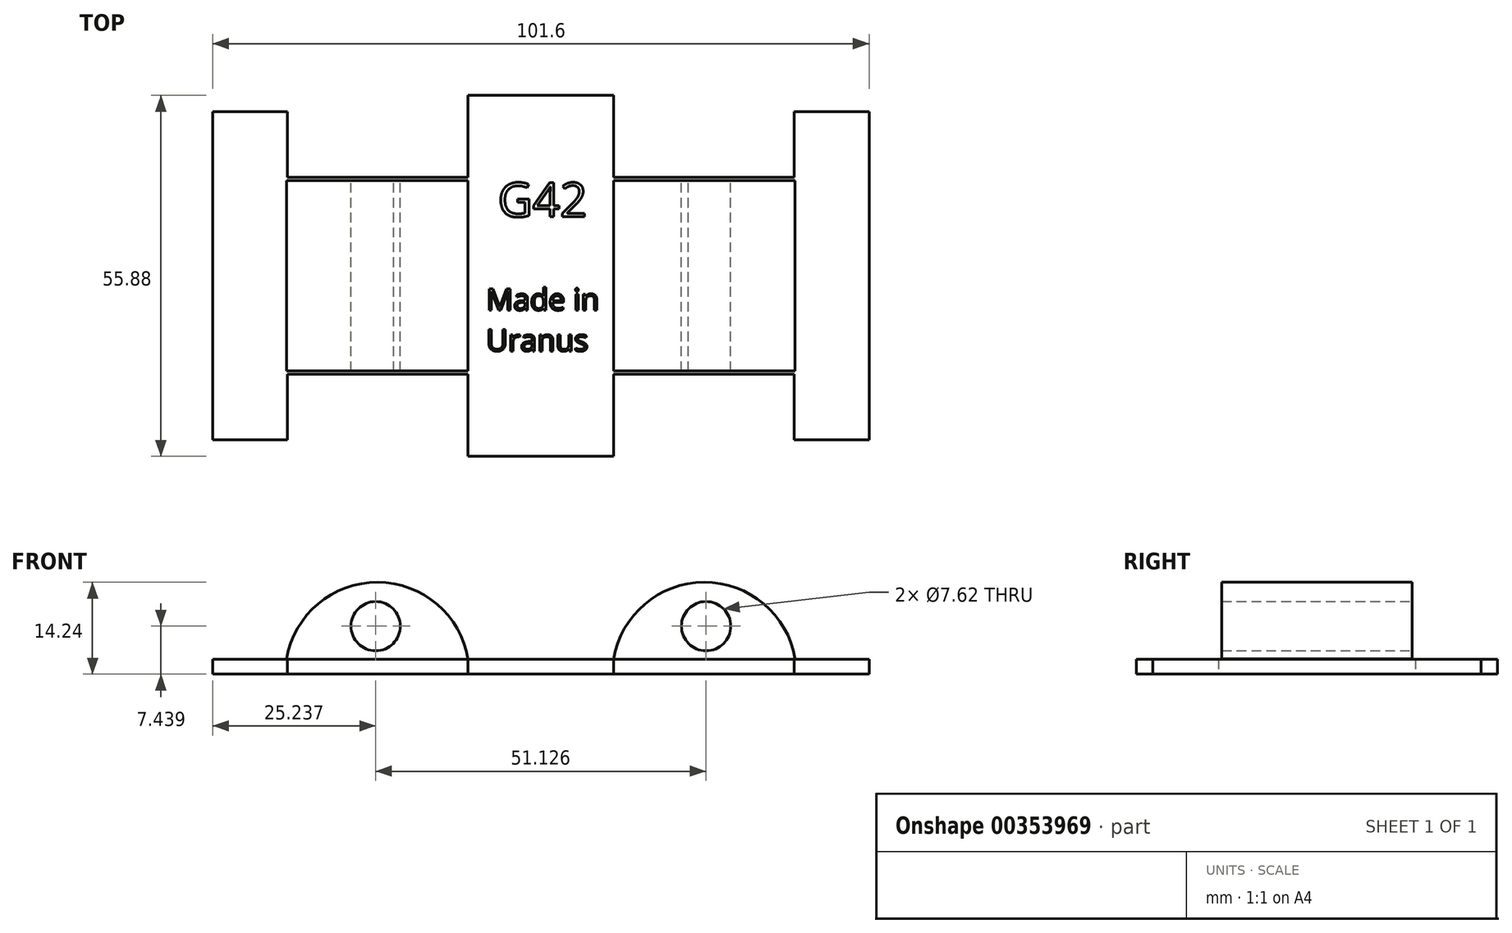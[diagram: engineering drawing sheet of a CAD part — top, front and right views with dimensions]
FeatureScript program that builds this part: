
annotation { "Feature Type Name" : "Feature", "Feature Type Description" : "" }
export const myFeature = defineFeature(function(context is Context, id is Id, definition is map)
    precondition{}
    {
        {
            var Q0;
            Q0=qCreatedBy(makeId("Top.planeOp"),FACE);
            var sketch = newSketch(context, id + "F0", { "sketchPlane" : qUnion([Q0])});
            skLineSegment(sketch, "E0.bottom", {"start": v(50.8, -25.4) * mm, "end": v(39.22, -25.4) * mm});
            skLineSegment(sketch, "E0.top", {"start": v(50.8, 25.4) * mm, "end": v(39.22, 25.4) * mm});
            skLineSegment(sketch, "E0.left", {"start": v(50.8, -25.4) * mm, "end": v(50.8, 25.4) * mm});
            skLineSegment(sketch, "E0.right", {"start": v(-50.8, -25.4) * mm, "end": v(-50.8, 25.4) * mm});
            skPoint(sketch, "E0.middle", {"position": v(0, 0) * mm});
            skLineSegment(sketch, "E1.left", {"start": v(-39.22, -25.4) * mm, "end": v(-39.22, -15.24) * mm});
            skLineSegment(sketch, "E1.right", {"start": v(-11.28, -25.4) * mm, "end": v(-11.28, -15.24) * mm});
            skLineSegment(sketch, "E2.trimOffspring", {"start": v(-39.22, -25.4) * mm, "end": v(-50.8, -25.4) * mm});
            skLineSegment(sketch, "E3", {"start": v(-39.22, -15.24) * mm, "end": v(-11.28, -15.24) * mm});
            skLineSegment(sketch, "E4.MirrorCS", {"start": v(-39.22, 15.24) * mm, "end": v(-11.28, 15.24) * mm});
            skLineSegment(sketch, "E5.MirrorCS", {"start": v(-11.28, 25.4) * mm, "end": v(-11.28, 15.24) * mm});
            skLineSegment(sketch, "E6.MirrorCS", {"start": v(-39.22, 25.4) * mm, "end": v(-39.22, 15.24) * mm});
            skLineSegment(sketch, "E7.MirrorCS", {"start": v(39.22, -15.24) * mm, "end": v(11.28, -15.24) * mm});
            skLineSegment(sketch, "E8.MirrorCS", {"start": v(11.28, -25.4) * mm, "end": v(11.28, -15.24) * mm});
            skLineSegment(sketch, "E9.MirrorCS", {"start": v(39.22, -25.4) * mm, "end": v(39.22, -15.24) * mm});
            skLineSegment(sketch, "E10.MirrorCS", {"start": v(39.22, 15.24) * mm, "end": v(11.28, 15.24) * mm});
            skLineSegment(sketch, "E11.MirrorCS", {"start": v(11.28, 25.4) * mm, "end": v(11.28, 15.24) * mm});
            skLineSegment(sketch, "E12.MirrorCS", {"start": v(39.22, 25.4) * mm, "end": v(39.22, 15.24) * mm});
            skLineSegment(sketch, "E13.trimOffspring", {"start": v(-39.22, 25.4) * mm, "end": v(-50.8, 25.4) * mm});
            skLineSegment(sketch, "E14.trimOffspring", {"start": v(11.28, 25.4) * mm, "end": v(-11.28, 25.4) * mm});
            skLineSegment(sketch, "E15.trimOffspring", {"start": v(11.28, -25.4) * mm, "end": v(-11.28, -25.4) * mm});
            skSolve(sketch);
        }
        {
            var Q0;
            Q0 = qSketchRegion(id + "F0", true);
            extrude(context, id + "F1", {"entities" : qUnion([Q0]), "depth" : 2.3 * mm});
        }
        {
            var Q0;
            Q0=qCreatedBy(makeId("Front.planeOp"),FACE);
            var sketch = newSketch(context, id + "F2", { "sketchPlane" : qUnion([Q0])});
            skArc(sketch, "E16", {"start": v(-11.24, 2.21) * mm, "mid": v(-25.22, 14.24) * mm, "end": v(-39.35, 2.4) * mm});
            skCircle(sketch, "E17", {"center": v(-25.56, 7.44) * mm, "radius": 3.81 * mm});
            skLineSegment(sketch, "E18", {"start": v(-39.35, 2.4) * mm, "end": v(-11.24, 2.21) * mm});
            skArc(sketch, "E19.MirrorCS", {"start": v(11.24, 2.21) * mm, "mid": v(25.22, 14.24) * mm, "end": v(39.35, 2.4) * mm});
            skCircle(sketch, "E20.MirrorC", {"center": v(25.56, 7.44) * mm, "radius": 3.81 * mm});
            skLineSegment(sketch, "E21.MirrorCS", {"start": v(39.35, 2.4) * mm, "end": v(11.24, 2.21) * mm});
            skSolve(sketch);
        }
        {
            var Q0;
            Q0 = qSketchRegion(id + "F2", true);
            extrude(context, id + "F3", {"entities" : qUnion([Q0]), "operationType" : NewBodyOperationType.ADD, "endBound" : BoundingType.SYMMETRIC, "depth" : 29.46 * mm});
        }
        {
            var Q0;
            Q0=makeQuery(id+"F1.opExtrude","CAP_FACE",FACE,{"disambiguationData":[OSD([sQuery(id+"F0.wireOp",EDGE,"E0.bottom"),sQuery(id+"F0.wireOp",EDGE,"E0.top"),sQuery(id+"F0.wireOp",EDGE,"E0.left"),sQuery(id+"F0.wireOp",EDGE,"E0.right"),sQuery(id+"F0.wireOp",EDGE,"E1.left"),sQuery(id+"F0.wireOp",EDGE,"E1.right"),sQuery(id+"F0.wireOp",EDGE,"E2.trimOffspring"),sQuery(id+"F0.wireOp",EDGE,"E3"),sQuery(id+"F0.wireOp",EDGE,"E4.MirrorCS"),sQuery(id+"F0.wireOp",EDGE,"E5.MirrorCS"),sQuery(id+"F0.wireOp",EDGE,"E6.MirrorCS"),sQuery(id+"F0.wireOp",EDGE,"E7.MirrorCS"),sQuery(id+"F0.wireOp",EDGE,"E8.MirrorCS"),sQuery(id+"F0.wireOp",EDGE,"E9.MirrorCS"),sQuery(id+"F0.wireOp",EDGE,"E10.MirrorCS"),sQuery(id+"F0.wireOp",EDGE,"E11.MirrorCS"),sQuery(id+"F0.wireOp",EDGE,"E12.MirrorCS"),sQuery(id+"F0.wireOp",EDGE,"E13.trimOffspring"),sQuery(id+"F0.wireOp",EDGE,"E14.trimOffspring"),sQuery(id+"F0.wireOp",EDGE,"E15.trimOffspring")])],"isStart":false});
            var sketch = newSketch(context, id + "F4", { "sketchPlane" : qUnion([Q0])});
            skText(sketch, "E22", { "text": "G42", "fontName": "OpenSans-Regular.ttf"});
            skText(sketch, "E23", { "text": "Made in\nUranus", "fontName": "OpenSans-Regular.ttf"});
            const initialGuessF4  = {"E22": [-0.00666, 0.00913, 1, 0, 0.00532], "E23": [-0.00847, -0.00532, 1, 0, 0.00335]};
            skSetInitialGuess(sketch, initialGuessF4);
            skSolve(sketch);
        }
        {
            var Q0;
            Q0 = qSketchRegion(id + "F4", true);
            extrude(context, id + "F5", {"entities" : qUnion([Q0]), "operationType" : NewBodyOperationType.ADD, "depth" : 0 * mm});
        }
        {
            var Q0;
            Q0=makeQuery(id+"F1.opExtrude","SWEPT_FACE",FACE,{"disambiguationData":[OSD([sQuery(id+"F0.wireOp",EDGE,"E14.trimOffspring")])]});
            var sketch = newSketch(context, id + "F6", { "sketchPlane" : qUnion([Q0])});
            skLineSegment(sketch, "E24.bottom", {"start": v(-11.28, 2.29) * mm, "end": v(11.28, 2.29) * mm});
            skLineSegment(sketch, "E24.top", {"start": v(-11.28, 0) * mm, "end": v(11.28, 0) * mm});
            skLineSegment(sketch, "E24.left", {"start": v(-11.28, 2.29) * mm, "end": v(-11.28, 0) * mm});
            skLineSegment(sketch, "E24.right", {"start": v(11.28, 2.29) * mm, "end": v(11.28, 0) * mm});
            skSolve(sketch);
        }
        {
            var Q0;
            Q0 = qSketchRegion(id + "F6", true);
            extrude(context, id + "F7", {"entities" : qUnion([Q0]), "operationType" : NewBodyOperationType.ADD, "depth" : 2.54 * mm});
        }
        {
            var Q0;
            Q0=makeQuery(id+"F1.opExtrude","SWEPT_FACE",FACE,{"disambiguationData":[OSD([sQuery(id+"F0.wireOp",EDGE,"E15.trimOffspring")])]});
            var sketch = newSketch(context, id + "F8", { "sketchPlane" : qUnion([Q0])});
            skLineSegment(sketch, "E25.bottom", {"start": v(-11.28, 2.29) * mm, "end": v(11.28, 2.29) * mm});
            skLineSegment(sketch, "E25.top", {"start": v(-11.28, 0) * mm, "end": v(11.28, 0) * mm});
            skLineSegment(sketch, "E25.left", {"start": v(-11.28, 2.29) * mm, "end": v(-11.28, 0) * mm});
            skLineSegment(sketch, "E25.right", {"start": v(11.28, 2.29) * mm, "end": v(11.28, 0) * mm});
            skSolve(sketch);
        }
        {
            var Q0;
            Q0 = qSketchRegion(id + "F8", true);
            extrude(context, id + "F9", {"entities" : qUnion([Q0]), "operationType" : NewBodyOperationType.ADD, "depth" : 2.54 * mm});
        }
    });
